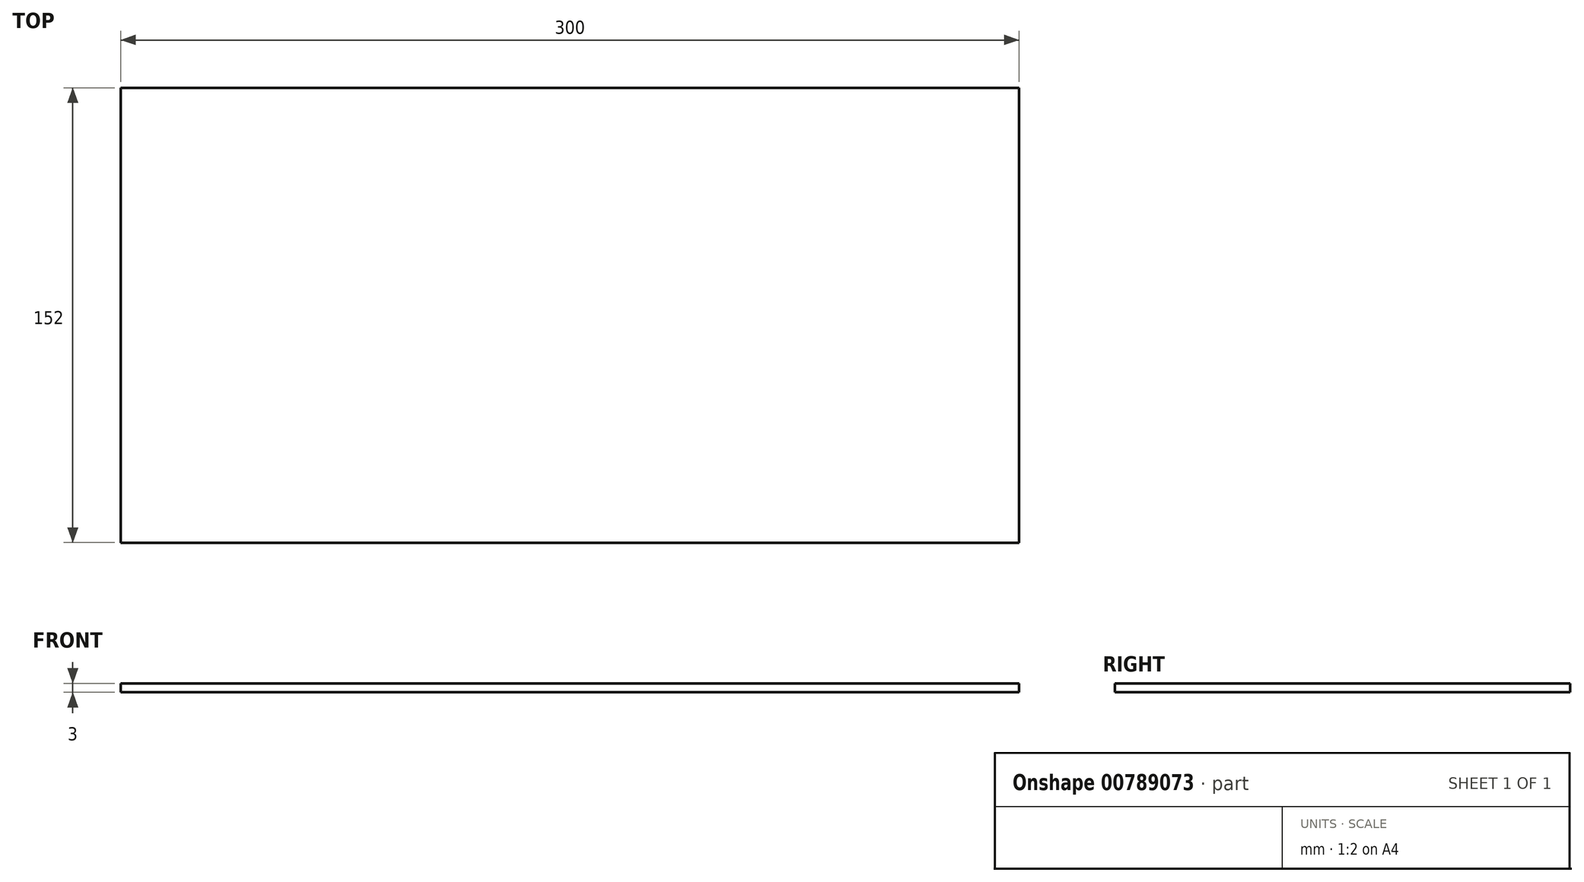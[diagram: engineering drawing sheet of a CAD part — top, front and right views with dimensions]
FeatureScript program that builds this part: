
annotation { "Feature Type Name" : "Feature", "Feature Type Description" : "" }
export const myFeature = defineFeature(function(context is Context, id is Id, definition is map)
    precondition{}
    {
        {
            var Q0;
            Q0=qCreatedBy(makeId("Top.planeOp"),FACE);
            var sketch = newSketch(context, id + "F0", { "sketchPlane" : qUnion([Q0])});
            skLineSegment(sketch, "E0.bottom", {"start": v(-147.52, 92.88) * mm, "end": v(152.48, 92.88) * mm});
            skLineSegment(sketch, "E0.top", {"start": v(-147.52, -59.12) * mm, "end": v(152.48, -59.12) * mm});
            skLineSegment(sketch, "E0.left", {"start": v(-147.52, 92.88) * mm, "end": v(-147.52, -59.12) * mm});
            skLineSegment(sketch, "E0.right", {"start": v(152.48, 92.88) * mm, "end": v(152.48, -59.12) * mm});
            skSolve(sketch);
        }
        {
            var Q0;
            Q0=makeQuery(id+"F0.imprint","IMPRINT",FACE,{"disambiguationData":[TD([[makeQuery(id+"F0.imprint","IMPRINT",EDGE,{"derivedFrom":sQuery(id+"F0.wireOp",EDGE,"E0.bottom")}),-1.0]])]});
            extrude(context, id + "F1", {"entities" : qUnion([Q0]), "depth" : 3 * mm, "offsetDistance" : 25 * mm});
        }
    });
